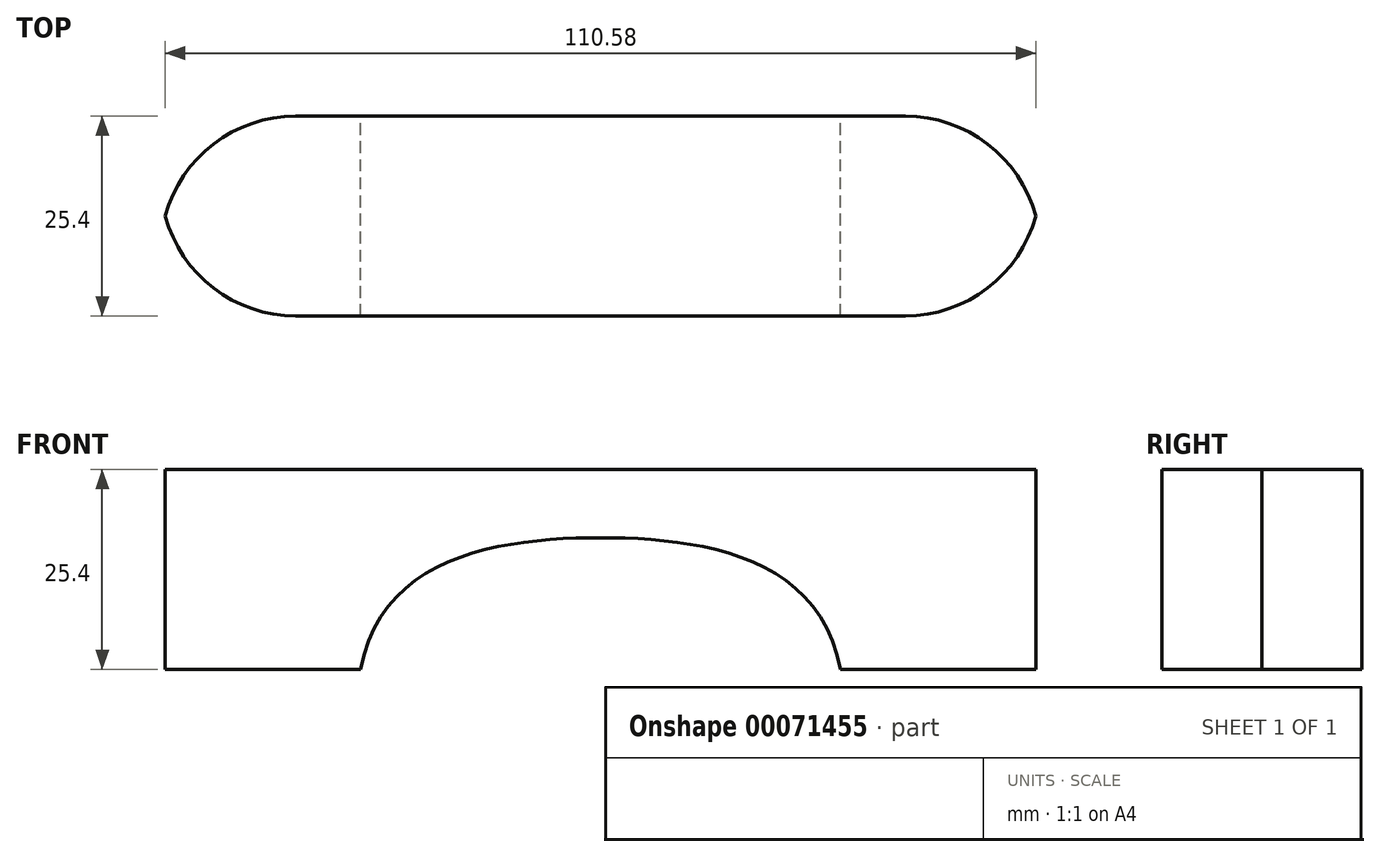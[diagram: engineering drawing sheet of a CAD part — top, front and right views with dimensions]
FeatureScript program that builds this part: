
annotation { "Feature Type Name" : "Feature", "Feature Type Description" : "" }
export const myFeature = defineFeature(function(context is Context, id is Id, definition is map)
    precondition{}
    {
        {
            var Q0;
            Q0=qCreatedBy(makeId("Front.planeOp"),FACE);
            var sketch = newSketch(context, id + "F0", { "sketchPlane" : qUnion([Q0])});
            skLineSegment(sketch, "E0", {"start": v(0, 0) * mm, "end": v(-55.88, 0) * mm});
            skLineSegment(sketch, "E1.MirrorCS", {"start": v(0, 0) * mm, "end": v(55.88, 0) * mm});
            skLineSegment(sketch, "E2", {"start": v(-55.88, 0) * mm, "end": v(-55.88, 25.4) * mm});
            skLineSegment(sketch, "E3.MirrorCS", {"start": v(55.88, 0) * mm, "end": v(55.88, 25.4) * mm});
            skLineSegment(sketch, "E4", {"start": v(-55.88, 25.4) * mm, "end": v(55.88, 25.4) * mm});
            skLineSegment(sketch, "E5", {"start": v(-55.88, 0) * mm, "end": v(-30.48, 0) * mm});
            skLineSegment(sketch, "E6.MirrorCS", {"start": v(55.88, 0) * mm, "end": v(30.48, 0) * mm});
            skFitSpline(sketch, "E7", {"points": [v(-30.48, 0) * mm, v(0, 16.73) * mm], "startDerivative": vector(8.19, 44.74) * mm, "endDerivative": vector(35.01, 0) * mm});
            skFitSpline(sketch, "E8.MirrorCS", {"points": [v(30.48, 0) * mm, v(0, 16.73) * mm], "startDerivative": vector(-8.19, 44.74) * mm, "endDerivative": vector(-35.01, 0) * mm});
            skSolve(sketch);
        }
        {
            var Q0;
            Q0=makeQuery(id+"F0.imprint","IMPRINT",FACE,{"disambiguationData":[TD([[makeQuery(id+"F0.imprint","IMPRINT",EDGE,{"derivedFrom":sQuery(id+"F0.wireOp",EDGE,"E2")}),-1.0]])]});
            extrude(context, id + "F1", {"entities" : qUnion([Q0]), "endBound" : BoundingType.SYMMETRIC, "depth" : 25.4 * mm});
        }
        {
            var Q0;
            Q0=makeQuery(id+"F1.opExtrude","CAP_EDGE",EDGE,{"disambiguationData":[OSD([sQuery(id+"F0.wireOp",EDGE,"E3.MirrorCS")])],"isStart":false});
            var Q1;
            Q1=makeQuery(id+"F1.opExtrude","CAP_EDGE",EDGE,{"disambiguationData":[OSD([sQuery(id+"F0.wireOp",EDGE,"E3.MirrorCS")])],"isStart":true});
            var Q2;
            Q2=makeQuery(id+"F1.opExtrude","CAP_EDGE",EDGE,{"disambiguationData":[OSD([sQuery(id+"F0.wireOp",EDGE,"E2")])],"isStart":false});
            var Q3;
            Q3=makeQuery(id+"F1.opExtrude","CAP_EDGE",EDGE,{"disambiguationData":[OSD([sQuery(id+"F0.wireOp",EDGE,"E2")])],"isStart":true});
            fillet(context, id + "F2", {"entities" : qUnion([Q0, Q1, Q2, Q3]), "radius" : 17.17 * mm, "tangentPropagation" : true, "allowEdgeOverflow" : false});
        }
    });
